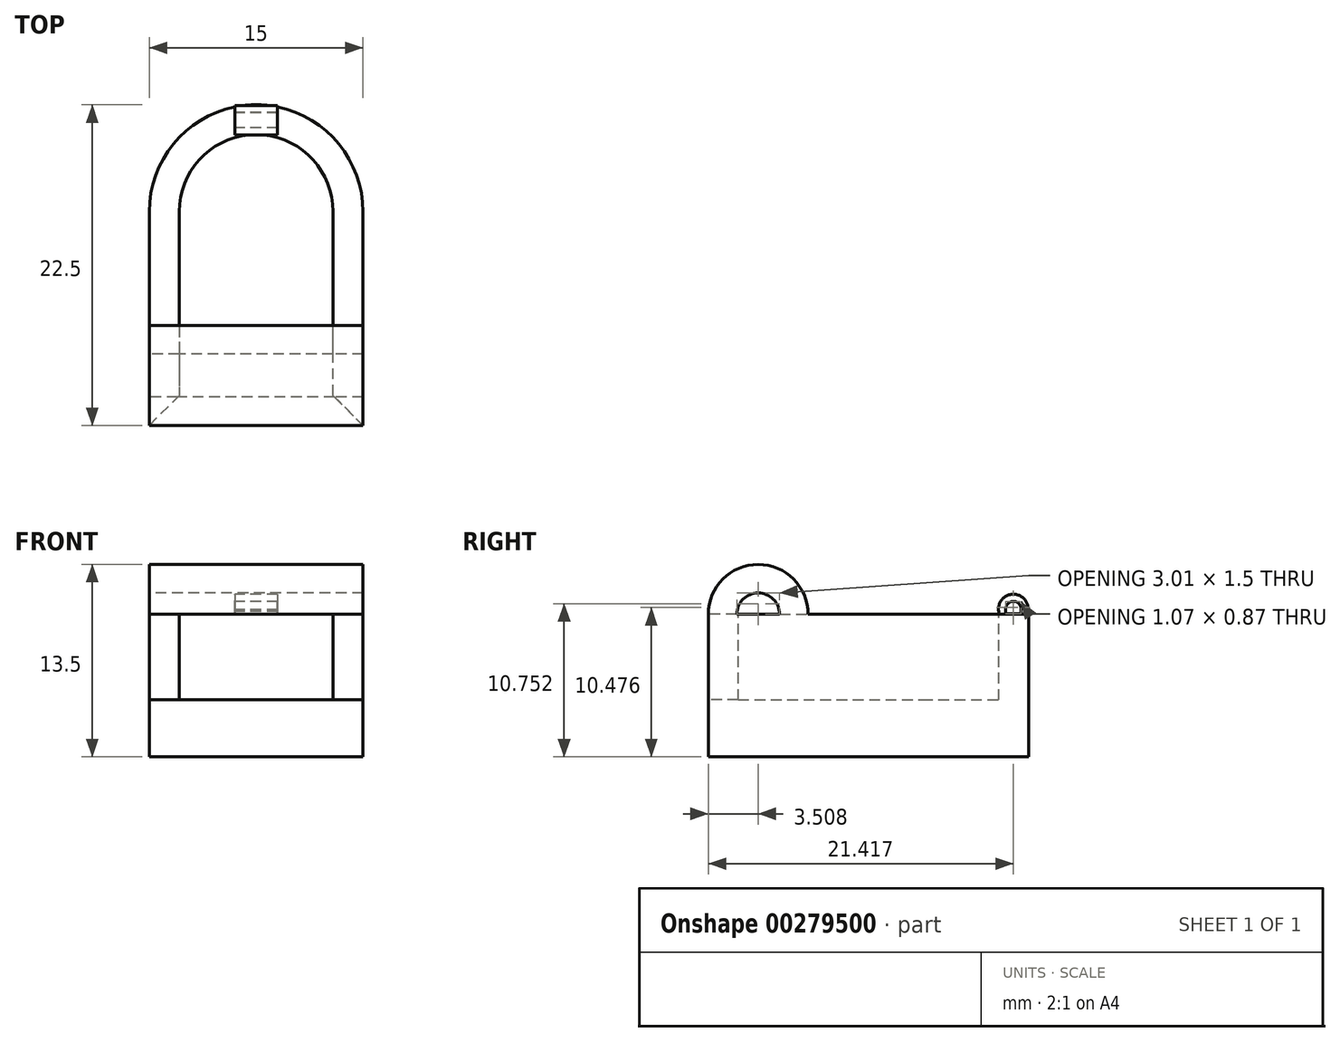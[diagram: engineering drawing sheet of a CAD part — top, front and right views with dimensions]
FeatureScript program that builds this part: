
annotation { "Feature Type Name" : "Feature", "Feature Type Description" : "" }
export const myFeature = defineFeature(function(context is Context, id is Id, definition is map)
    precondition{}
    {
        {
            var Q0;
            Q0=qCreatedBy(makeId("Top.planeOp"),FACE);
            var sketch = newSketch(context, id + "F0", { "sketchPlane" : qUnion([Q0])});
            skLineSegment(sketch, "E0.bottom", {"start": v(-16.9, 9.46) * mm, "end": v(-1.9, 9.46) * mm});
            skLineSegment(sketch, "E0.top", {"start": v(-16.9, -5.54) * mm, "end": v(-1.9, -5.54) * mm});
            skLineSegment(sketch, "E0.left", {"start": v(-16.9, 9.46) * mm, "end": v(-16.9, -5.54) * mm});
            skLineSegment(sketch, "E0.right", {"start": v(-1.9, 9.46) * mm, "end": v(-1.9, -5.54) * mm});
            skArc(sketch, "E1", {"start": v(-1.9, 9.46) * mm, "mid": v(-9.4, 16.96) * mm, "end": v(-16.9, 9.46) * mm});
            skSolve(sketch);
        }
        {
            var Q0;
            Q0 = qSketchRegion(id + "F0", true);
            extrude(context, id + "F1", {"entities" : qUnion([Q0]), "depth" : 10 * mm});
        }
        {
            var Q0;
            Q0=makeQuery(id+"F1.opExtrude","CAP_FACE",FACE,{"disambiguationData":[OSD([sQuery(id+"F0.wireOp",EDGE,"E0.top"),sQuery(id+"F0.wireOp",EDGE,"E0.left"),sQuery(id+"F0.wireOp",EDGE,"E0.right"),sQuery(id+"F0.wireOp",EDGE,"E1")])],"isStart":false});
            var sketch = newSketch(context, id + "F2", { "sketchPlane" : qUnion([Q0])});
            skLineSegment(sketch, "E2.0", {"start": v(-14.8, 9.46) * mm, "end": v(-14.8, -3.44) * mm});
            skArc(sketch, "E2.1", {"start": v(-4, 9.46) * mm, "mid": v(-9.4, 14.86) * mm, "end": v(-14.8, 9.46) * mm});
            skLineSegment(sketch, "E2.2", {"start": v(-4, -3.44) * mm, "end": v(-4, 9.46) * mm});
            skLineSegment(sketch, "E3", {"start": v(-4, -3.44) * mm, "end": v(-1.9, -5.54) * mm});
            skLineSegment(sketch, "E4", {"start": v(-1.9, -5.54) * mm, "end": v(-16.9, -5.54) * mm});
            skLineSegment(sketch, "E5", {"start": v(-16.9, -5.54) * mm, "end": v(-14.8, -3.44) * mm});
            skSolve(sketch);
        }
        {
            var Q0;
            Q0 = qSketchRegion(id + "F2", true);
            extrude(context, id + "F3", {"entities" : qUnion([Q0]), "operationType" : NewBodyOperationType.REMOVE, "oppositeDirection" : true, "depth" : 6 * mm});
        }
        {
            var Q0;
            Q0=makeQuery(id+"F1.opExtrude","SWEPT_FACE",FACE,{"disambiguationData":[OSD([sQuery(id+"F0.wireOp",EDGE,"E0.left")])]});
            var sketch = newSketch(context, id + "F4", { "sketchPlane" : qUnion([Q0])});
            skArc(sketch, "E6", {"start": v(5.54, 10) * mm, "mid": v(2.03, 13.5) * mm, "end": v(-1.47, 10) * mm});
            skLineSegment(sketch, "E7.0", {"start": v(3.54, 10) * mm, "end": v(3.54, 10) * mm});
            skArc(sketch, "E8.0", {"start": v(3.54, 10) * mm, "mid": v(2.03, 11.5) * mm, "end": v(0.53, 10) * mm});
            skSolve(sketch);
        }
        {
            var Q0;
            {var subQ0=sQuery(id+"F4.wireOp",EDGE,"E6");Q0=makeQuery(id+"F4.imprint","IMPRINT",FACE,{"disambiguationData":[TD([[makeQuery(id+"F4.imprint","IMPRINT",EDGE,{"derivedFrom":subQ0}),1.0]])]});}
            var Q1;
            Q1=makeQuery(id+"F1.opExtrude","SWEPT_FACE",FACE,{"disambiguationData":[OSD([sQuery(id+"F0.wireOp",EDGE,"E0.right")])]});
            extrude(context, id + "F5", {"entities" : qUnion([Q0]), "operationType" : NewBodyOperationType.ADD, "endBound" : BoundingType.UP_TO_SURFACE, "oppositeDirection" : true, "endBoundEntityFace" : qUnion([Q1]), "depth" : 25 * mm});
        }
        {
            var Q0;
            {var subQ0=sQuery(id+"F0.wireOp",EDGE,"E0.left");Q0=makeQuery(id+"F5.boolean.opBoolean","MERGE",FACE,{"derivedFrom":[makeQuery(id+"F1.opExtrude","SWEPT_FACE",FACE,{"disambiguationData":[OSD([subQ0])]}),makeQuery(id+"F5.opExtrude","CAP_FACE",FACE,{"disambiguationData":[OSD([subQ0,sQuery(id+"F4.wireOp",EDGE,"E6"),sQuery(id+"F4.wireOp",EDGE,"E8.0")])],"isStart":true})]});}
            cPlane(context, id + "F6", {"entities" : qUnion([Q0]), "cplaneType" : CPlaneType.OFFSET, "offset" : 6 * mm, "oppositeDirection" : true, "width" : 150 * mm, "height" : 150 * mm});
        }
        {
            var Q0;
            Q0=qCreatedBy(id+"F6.planeOp",FACE);
            var sketch = newSketch(context, id + "F7", { "sketchPlane" : qUnion([Q0])});
            skArc(sketch, "E9", {"start": v(-15.35, 10.3) * mm, "mid": v(-15.87, 10.91) * mm, "end": v(-16.41, 10.32) * mm});
            skArc(sketch, "E10.0", {"start": v(-14.85, 10.22) * mm, "mid": v(-15.85, 11.41) * mm, "end": v(-16.91, 10.26) * mm});
            skLineSegment(sketch, "E11", {"start": v(-16.91, 10) * mm, "end": v(-16.91, 10.26) * mm});
            skLineSegment(sketch, "E12", {"start": v(-14.85, 10.22) * mm, "end": v(-14.85, 10) * mm});
            skLineSegment(sketch, "E13", {"start": v(-14.85, 10) * mm, "end": v(-16.91, 10) * mm});
            skLineSegment(sketch, "E14", {"start": v(-16.41, 10.32) * mm, "end": v(-16.41, 10.04) * mm});
            skLineSegment(sketch, "E15", {"start": v(-16.41, 10.04) * mm, "end": v(-15.34, 10.04) * mm});
            skLineSegment(sketch, "E16", {"start": v(-15.34, 10.04) * mm, "end": v(-15.35, 10.3) * mm});
            skSolve(sketch);
        }
        {
            var Q0;
            Q0 = qSketchRegion(id + "F7", true);
            extrude(context, id + "F8", {"entities" : qUnion([Q0]), "oppositeDirection" : true, "depth" : 3 * mm});
        }
    });
